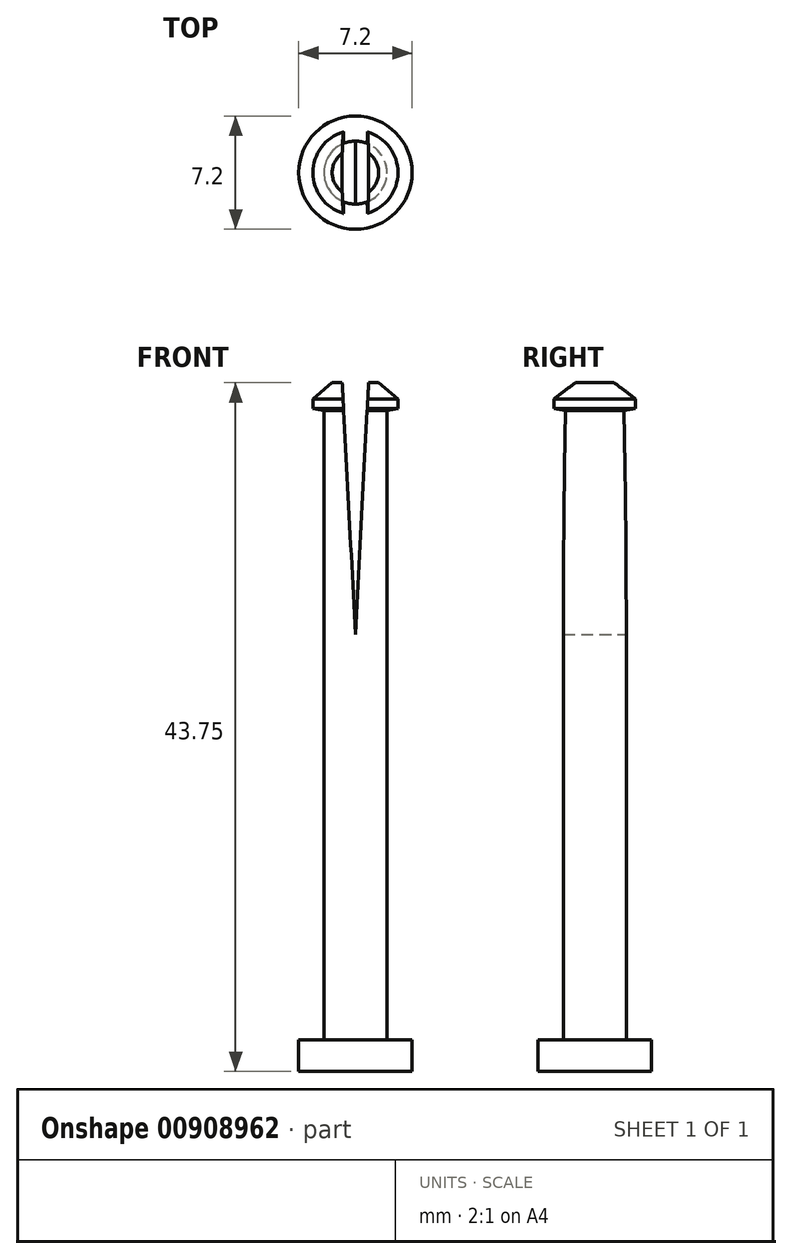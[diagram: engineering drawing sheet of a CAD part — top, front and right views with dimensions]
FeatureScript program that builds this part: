
annotation { "Feature Type Name" : "Feature", "Feature Type Description" : "" }
export const myFeature = defineFeature(function(context is Context, id is Id, definition is map)
    precondition{}
    {
        {
            var Q0;
            Q0=qCreatedBy(makeId("Front.planeOp"),FACE);
            var sketch = newSketch(context, id + "F0", { "sketchPlane" : qUnion([Q0])});
            skLineSegment(sketch, "E0", {"start": v(-1.48, 43.75) * mm, "end": v(-2.7, 42.72) * mm});
            skLineSegment(sketch, "E1", {"start": v(-2.7, 42.72) * mm, "end": v(-2.7, 42.12) * mm});
            skLineSegment(sketch, "E2", {"start": v(-2.7, 42.12) * mm, "end": v(-2, 42) * mm});
            skLineSegment(sketch, "E3", {"start": v(-2, 42) * mm, "end": v(-2, 2) * mm});
            skLineSegment(sketch, "E4", {"start": v(-2, 2) * mm, "end": v(-3.6, 2) * mm});
            skLineSegment(sketch, "E5", {"start": v(-3.6, 2) * mm, "end": v(-3.6, 0) * mm});
            skLineSegment(sketch, "E6", {"start": v(-3.6, 0) * mm, "end": v(0, 0) * mm});
            skLineSegment(sketch, "E7", {"start": v(-1.48, 43.75) * mm, "end": v(0, 43.75) * mm});
            skLineSegment(sketch, "E8", {"start": v(0, 43.75) * mm, "end": v(0, 0) * mm});
            skLineSegment(sketch, "E9", {"start": v(0, 16.3) * mm, "end": v(0, -18.79) * mm, "construction": true});
            skSolve(sketch);
        }
        {
            var Q0;
            Q0=qCreatedBy(makeId("Front.planeOp"),FACE);
            var sketch = newSketch(context, id + "F1", { "sketchPlane" : qUnion([Q0])});
            skLineSegment(sketch, "E10", {"start": v(-0.84, 43.75) * mm, "end": v(0, 27.75) * mm});
            skLineSegment(sketch, "E11", {"start": v(0, 27.75) * mm, "end": v(0.84, 43.75) * mm});
            skLineSegment(sketch, "E12", {"start": v(0.84, 43.75) * mm, "end": v(-0.84, 43.75) * mm});
            skSolve(sketch);
        }
        {
            var Q0;
            Q0=makeQuery(id+"F0.imprint","IMPRINT",FACE,{"disambiguationData":[TD([[makeQuery(id+"F0.imprint","IMPRINT",EDGE,{"derivedFrom":sQuery(id+"F0.wireOp",EDGE,"E0")}),1.0]])]});
            var Q1;
            Q1=sQuery(id+"F0.wireOp",EDGE,"8SHG9E29-969J-Fn0P-8r8L-7sNdC3JjfOIx");
            var Q2;
            Q2=sQuery(id+"F0.wireOp",EDGE,"E9");
            revolve(context, id + "F2", {"surfaceOperationType" : NewSurfaceOperationType.NEW, "entities" : qUnion([Q0]), "surfaceEntities" : qUnion([Q1]), "axis" : qUnion([Q2]), "revolveType" : RevolveType.FULL});
        }
        {
            var Q0;
            Q0=makeQuery(id+"F1.imprint","IMPRINT",FACE,{"disambiguationData":[TD([[makeQuery(id+"F1.imprint","IMPRINT",EDGE,{"derivedFrom":sQuery(id+"F1.wireOp",EDGE,"E10")}),1.0]])]});
            extrude(context, id + "F3", {"entities" : qUnion([Q0]), "depth" : 4 * mm, "offsetDistance" : 25 * mm, "hasSecondDirection" : true, "secondDirectionOppositeDirection" : true, "secondDirectionDepth" : 4 * mm});
        }
        {
            var Q0;
            Q0=makeQuery(id+"F3.opExtrude","SWEPT_BODY",BODY,{"disambiguationData":[OSD([sQuery(id+"F1.wireOp",EDGE,"E10"),sQuery(id+"F1.wireOp",EDGE,"E11"),sQuery(id+"F1.wireOp",EDGE,"E12")])]});
            var Q1;
            Q1=makeQuery(id+"F2.opRevolve","SWEPT_BODY",BODY,{"disambiguationData":[OSD([sQuery(id+"F0.wireOp",EDGE,"E0"),sQuery(id+"F0.wireOp",EDGE,"E1"),sQuery(id+"F0.wireOp",EDGE,"E2"),sQuery(id+"F0.wireOp",EDGE,"E3"),sQuery(id+"F0.wireOp",EDGE,"E4"),sQuery(id+"F0.wireOp",EDGE,"E5"),sQuery(id+"F0.wireOp",EDGE,"E6"),sQuery(id+"F0.wireOp",EDGE,"E7"),sQuery(id+"F0.wireOp",EDGE,"E8")])]});
            booleanBodies(context, id + "F4", {"operationType" : BooleanOperationType.SUBTRACTION, "tools" : qUnion([Q0]), "targets" : qUnion([Q1])});
        }
    });
